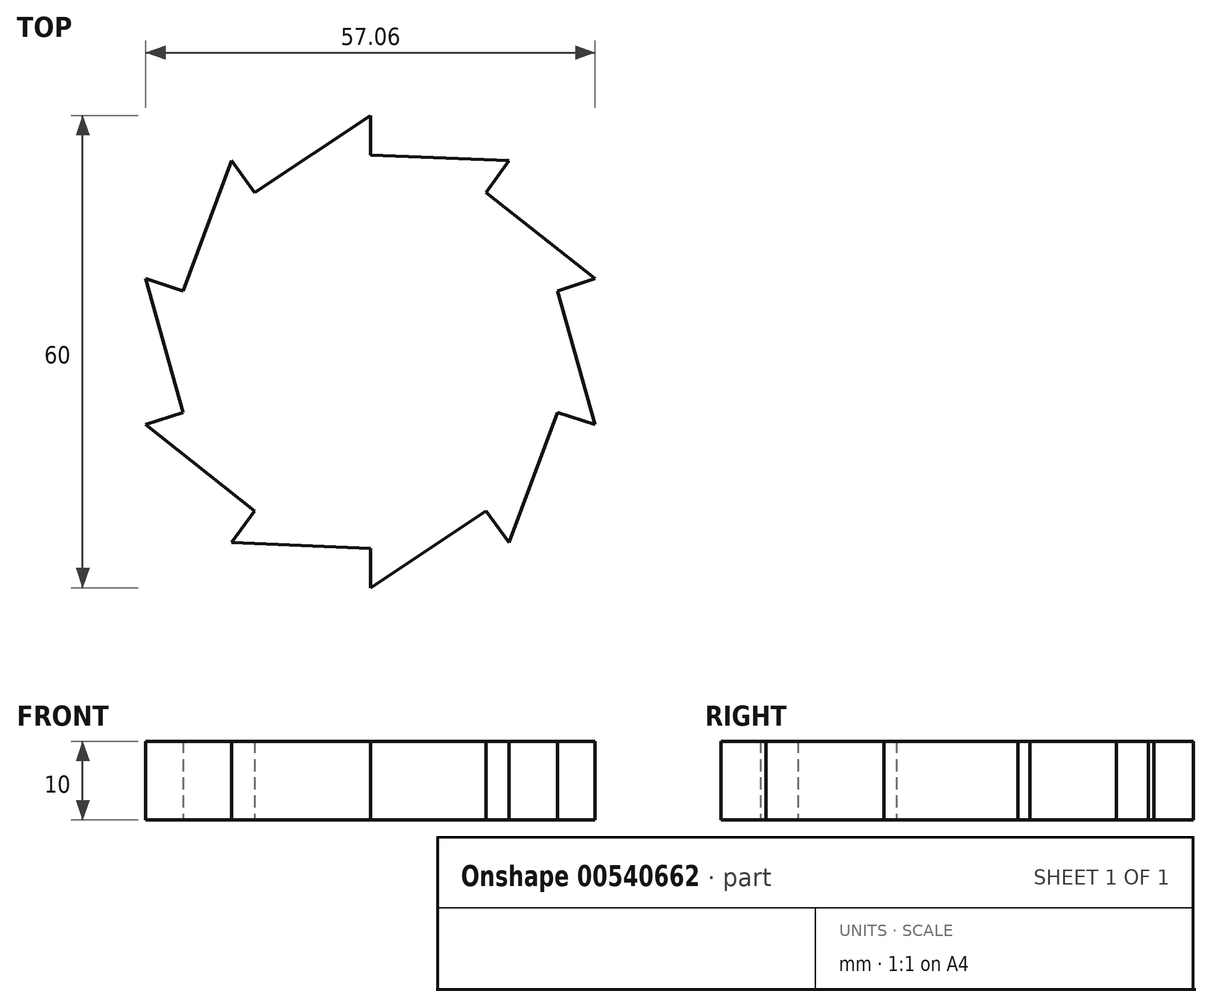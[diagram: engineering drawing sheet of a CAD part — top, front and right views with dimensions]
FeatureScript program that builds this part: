
annotation { "Feature Type Name" : "Feature", "Feature Type Description" : "" }
export const myFeature = defineFeature(function(context is Context, id is Id, definition is map)
    precondition{}
    {
        {
            var Q0;
            Q0=qCreatedBy(makeId("Top.planeOp"),FACE);
            var sketch = newSketch(context, id + "F0", { "sketchPlane" : qUnion([Q0])});
            skLineSegment(sketch, "E0", {"start": v(0, 30) * mm, "end": v(0, 30) * mm});
            skLineSegment(sketch, "E1", {"start": v(0, 30) * mm, "end": v(0, 25) * mm});
            skLineSegment(sketch, "E2", {"start": v(0, 25) * mm, "end": v(17.63, 24.27) * mm});
            skLineSegment(sketch, "E3.1.0", {"start": v(-17.63, 24.27) * mm, "end": v(-14.7, 20.23) * mm});
            skLineSegment(sketch, "E3.1.1", {"start": v(-14.7, 20.23) * mm, "end": v(0, 30) * mm});
            skLineSegment(sketch, "E3.2.0", {"start": v(-28.53, 9.27) * mm, "end": v(-23.78, 7.73) * mm});
            skLineSegment(sketch, "E3.2.1", {"start": v(-23.78, 7.73) * mm, "end": v(-17.63, 24.27) * mm});
            skLineSegment(sketch, "E4.2.3.0", {"start": v(-28.53, -9.27) * mm, "end": v(-23.78, -7.73) * mm});
            skLineSegment(sketch, "E4.3.3.0", {"start": v(-23.78, -7.73) * mm, "end": v(-28.53, 9.27) * mm});
            skLineSegment(sketch, "E4.2.4.0", {"start": v(-17.63, -24.27) * mm, "end": v(-14.7, -20.23) * mm});
            skLineSegment(sketch, "E4.3.4.0", {"start": v(-14.7, -20.23) * mm, "end": v(-28.53, -9.27) * mm});
            skLineSegment(sketch, "E4.2.5.0", {"start": v(0, -30) * mm, "end": v(0, -25) * mm});
            skLineSegment(sketch, "E4.3.5.0", {"start": v(0, -25) * mm, "end": v(-17.63, -24.27) * mm});
            skLineSegment(sketch, "E4.2.6.0", {"start": v(17.63, -24.27) * mm, "end": v(14.7, -20.23) * mm});
            skLineSegment(sketch, "E4.3.6.0", {"start": v(14.7, -20.23) * mm, "end": v(0, -30) * mm});
            skLineSegment(sketch, "E4.2.7.0", {"start": v(28.53, -9.27) * mm, "end": v(23.78, -7.73) * mm});
            skLineSegment(sketch, "E4.3.7.0", {"start": v(23.78, -7.73) * mm, "end": v(17.63, -24.27) * mm});
            skLineSegment(sketch, "E4.2.8.0", {"start": v(28.53, 9.27) * mm, "end": v(23.78, 7.73) * mm});
            skLineSegment(sketch, "E4.3.8.0", {"start": v(23.78, 7.73) * mm, "end": v(28.53, -9.27) * mm});
            skLineSegment(sketch, "E4.2.9.0", {"start": v(17.63, 24.27) * mm, "end": v(14.7, 20.23) * mm});
            skLineSegment(sketch, "E4.3.9.0", {"start": v(14.7, 20.23) * mm, "end": v(28.53, 9.27) * mm});
            skLineSegment(sketch, "E5.trimOffspring", {"start": v(-17.63, 24.27) * mm, "end": v(-17.63, 24.27) * mm});
            skLineSegment(sketch, "E6.trimOffspring", {"start": v(-28.53, 9.27) * mm, "end": v(-28.53, 9.27) * mm});
            skLineSegment(sketch, "E7.trimOffspring", {"start": v(0, -30) * mm, "end": v(0, -30) * mm});
            skLineSegment(sketch, "E8.trimOffspring", {"start": v(17.63, -24.27) * mm, "end": v(17.63, -24.27) * mm});
            skLineSegment(sketch, "E9.trimOffspring", {"start": v(28.53, -9.27) * mm, "end": v(28.53, -9.27) * mm});
            skLineSegment(sketch, "E10.trimOffspring", {"start": v(28.53, 9.27) * mm, "end": v(28.53, 9.27) * mm});
            skSolve(sketch);
        }
        {
            var Q0;
            Q0=makeQuery(id+"F0.imprint","IMPRINT",FACE,{"disambiguationData":[TD([[makeQuery(id+"F0.imprint","IMPRINT",EDGE,{"derivedFrom":sQuery(id+"F0.wireOp",EDGE,"E1")}),-1.0]])]});
            extrude(context, id + "F1", {"entities" : qUnion([Q0]), "depth" : 10 * mm, "offsetDistance" : 25 * mm});
        }
    });
